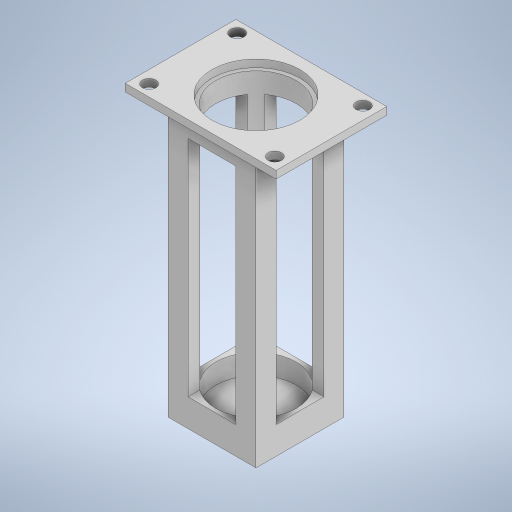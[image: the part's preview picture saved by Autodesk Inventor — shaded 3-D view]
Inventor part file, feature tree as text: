
AUTODESK INVENTOR PART (.ipt)
format: ipt  version: 2023.5 (Build 275446000, 446)  size: 330,752 bytes
history: native  units: in
note: dims shown in document units (in); Inventor stores cm internally (conversion verified against a paired STEP export)
features: extrude x5, sketch x5
ambient origin geometry x8: Origin, YZ Plane, XZ Plane, XY Plane, X Axis, Y Axis, Z Axis, Center Point
bodies: Solid1 (feature_tree)
feature tree (10):
  extrude  "Extrusion1"  Depth=1.378in
  extrude  "Extrusion2"  Depth=4.1339in TaperAngle=0.0deg
  extrude  "Extrusion3"  Depth=0.315in
  extrude  "Extrusion4"  Depth=0.315in
  extrude  "Extrusion5"  Depth=0.315in
  sketch  "Sketch1"  dims[d0=1.378in d1=1.378in]
  sketch  "Sketch2"  dims[d2=1.2598in d3=4.1339in d4=0.0in]
  sketch  "Sketch3"  dims[d5=0.315in d6=0.315in]
  sketch  "Sketch4"  dims[d7=0.315in d8=0.315in]
  sketch  "Sketch5"  dims[d9=0.0in d10=0.0in d11=0.315in d12=0.315in d13=0.315in d14=0.315in d15=0.0in d16=0.0in d17=0.1181in d18=0.0in d19=2.3622in d20=1.7323in d21=1.378in d22=0.2126in d23=0.1772in d24=0.1969in d25=0.2126in d26=0.1772in d27=0.1969in d28=0.1772in d29=0.1969in d30=0.2126in d31=0.2126in d32=0.1772in d33=0.1969in d34=0.1181in d35=0.0in]
